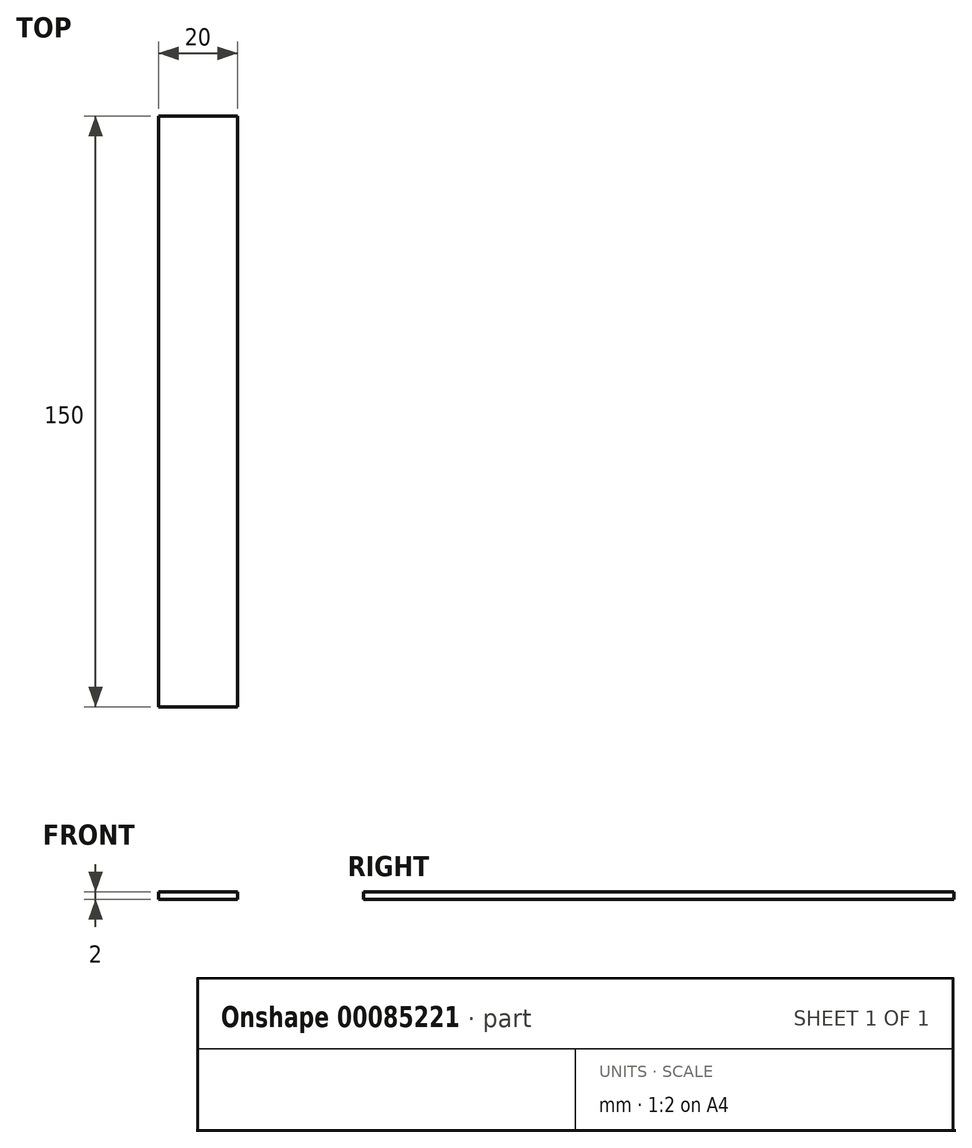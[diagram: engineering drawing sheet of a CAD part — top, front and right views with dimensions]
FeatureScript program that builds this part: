
annotation { "Feature Type Name" : "Feature", "Feature Type Description" : "" }
export const myFeature = defineFeature(function(context is Context, id is Id, definition is map)
    precondition{}
    {
        {
            var Q0;
            Q0=qCreatedBy(makeId("Right.planeOp"),FACE);
            var sketch = newSketch(context, id + "F0", { "sketchPlane" : qUnion([Q0])});
            skLineSegment(sketch, "E0", {"start": v(0, 44.77) * mm, "end": v(0, -54.3) * mm, "construction": true});
            skLineSegment(sketch, "E1", {"start": v(-66.71, 0) * mm, "end": v(70.82, 0) * mm, "construction": true});
            skLineSegment(sketch, "E2.bottom", {"start": v(-75, 1) * mm, "end": v(75, 1) * mm});
            skLineSegment(sketch, "E2.top", {"start": v(-75, -1) * mm, "end": v(75, -1) * mm});
            skLineSegment(sketch, "E2.left", {"start": v(-75, 1) * mm, "end": v(-75, -1) * mm});
            skLineSegment(sketch, "E2.right", {"start": v(75, 1) * mm, "end": v(75, -1) * mm});
            skLineSegment(sketch, "E3", {"start": v(-75, -1) * mm, "end": v(75, 1) * mm, "construction": true});
            skLineSegment(sketch, "E4", {"start": v(-75, 1) * mm, "end": v(75, -1) * mm, "construction": true});
            skPoint(sketch, "E5", {"position": v(0, 0) * mm});
            skSolve(sketch);
        }
        {
            var Q0;
            Q0 = qSketchRegion(id + "F0", true);
            extrude(context, id + "F1", {"entities" : qUnion([Q0]), "endBound" : BoundingType.SYMMETRIC, "depth" : 20 * mm});
        }
    });
